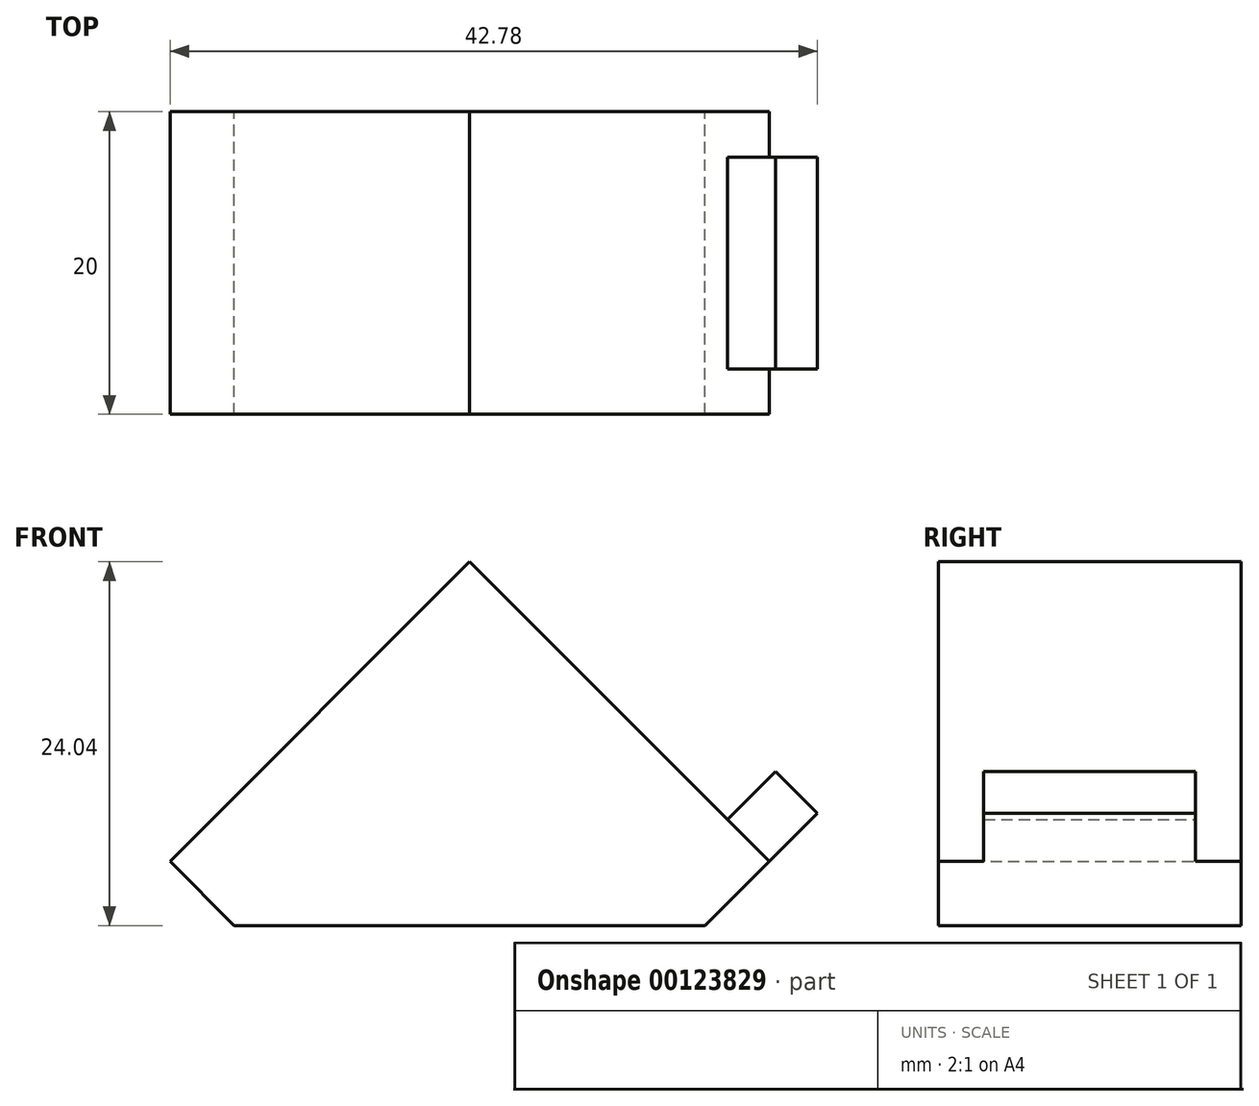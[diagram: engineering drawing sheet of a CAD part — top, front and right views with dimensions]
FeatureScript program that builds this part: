
annotation { "Feature Type Name" : "Feature", "Feature Type Description" : "" }
export const myFeature = defineFeature(function(context is Context, id is Id, definition is map)
    precondition{}
    {
        {
            var Q0;
            Q0=qCreatedBy(makeId("Front.planeOp"),FACE);
            var sketch = newSketch(context, id + "F0", { "sketchPlane" : qUnion([Q0])});
            skLineSegment(sketch, "E0", {"start": v(19.8, 4.24) * mm, "end": v(0, 24.04) * mm});
            skLineSegment(sketch, "E1", {"start": v(0, 24.04) * mm, "end": v(0, 0) * mm, "construction": true});
            skLineSegment(sketch, "E2", {"start": v(0, 0) * mm, "end": v(15.56, 0) * mm});
            skLineSegment(sketch, "E3", {"start": v(19.8, 4.24) * mm, "end": v(15.56, 0) * mm});
            skLineSegment(sketch, "E4.MirrorCS", {"start": v(-19.8, 4.24) * mm, "end": v(0, 24.04) * mm});
            skLineSegment(sketch, "E5.MirrorCS", {"start": v(-19.8, 4.24) * mm, "end": v(-15.56, 0) * mm});
            skLineSegment(sketch, "E6.MirrorCS", {"start": v(0, 0) * mm, "end": v(-15.56, 0) * mm});
            skSolve(sketch);
        }
        {
            var Q0;
            Q0=makeQuery(id+"F0.imprint","IMPRINT",FACE,{"disambiguationData":[TD([[makeQuery(id+"F0.imprint","IMPRINT",EDGE,{"derivedFrom":sQuery(id+"F0.wireOp",EDGE,"E0")}),1.0]])]});
            extrude(context, id + "F1", {"entities" : qUnion([Q0]), "depth" : 20 * mm});
        }
        {
            var Q0;
            Q0=makeQuery(id+"F1.opExtrude","SWEPT_FACE",FACE,{"disambiguationData":[OSD([sQuery(id+"F0.wireOp",EDGE,"E0")])]});
            var sketch = newSketch(context, id + "F2", { "sketchPlane" : qUnion([Q0])});
            skLineSegment(sketch, "E7", {"start": v(5, -2.42) * mm, "end": v(5, -17.05) * mm, "construction": true});
            skLineSegment(sketch, "E8", {"start": v(-17, -10) * mm, "end": v(11, -10) * mm, "construction": true});
            skPoint(sketch, "E9", {"position": v(5, -10) * mm});
            skCircle(sketch, "E10", {"center": v(5, -10) * mm, "radius": 4 * mm});
            skCircle(sketch, "E11", {"center": v(5, -10) * mm, "radius": 2.25 * mm});
            skLineSegment(sketch, "E12.bottom", {"start": v(-17, -7.1) * mm, "end": v(-3, -7.1) * mm});
            skLineSegment(sketch, "E12.top", {"start": v(-17, -12.9) * mm, "end": v(-3, -12.9) * mm});
            skLineSegment(sketch, "E12.left", {"start": v(-17, -7.1) * mm, "end": v(-17, -12.9) * mm});
            skLineSegment(sketch, "E12.right", {"start": v(-3, -7.1) * mm, "end": v(-3, -12.9) * mm});
            skPoint(sketch, "E12.middle", {"position": v(-10, -10) * mm});
            skSolve(sketch);
        }
        {
            var Q0;
            Q0=makeQuery(id+"F2.imprint","IMPRINT",FACE,{"disambiguationData":[TD([[makeQuery(id+"F2.imprint","IMPRINT",EDGE,{"derivedFrom":sQuery(id+"F2.wireOp",EDGE,"E12.bottom")}),-1.0]])]});
            extrude(context, id + "F3", {"entities" : qUnion([Q0]), "operationType" : NewBodyOperationType.ADD, "depth" : 4.5 * mm});
        }
        {
            var Q0;
            Q0=makeQuery(id+"F2.imprint","IMPRINT",FACE,{"disambiguationData":[TD([[makeQuery(id+"F2.imprint","IMPRINT",EDGE,{"derivedFrom":sQuery(id+"F2.wireOp",EDGE,"E10")}),1.0]])]});
            extrude(context, id + "F4", {"entities" : qUnion([Q0]), "operationType" : NewBodyOperationType.REMOVE, "endBound" : BoundingType.THROUGH_ALL, "oppositeDirection" : true, "depth" : 25 * mm, "hasSecondDirection" : true, "secondDirectionOppositeDirection" : true, "secondDirectionDepth" : 6 * mm});
        }
        {
            var Q0;
            Q0=makeQuery(id+"F2.imprint","IMPRINT",FACE,{"disambiguationData":[TD([[makeQuery(id+"F2.imprint","IMPRINT",EDGE,{"derivedFrom":sQuery(id+"F2.wireOp",EDGE,"E11")}),1.0]])]});
            extrude(context, id + "F5", {"entities" : qUnion([Q0]), "operationType" : NewBodyOperationType.REMOVE, "endBound" : BoundingType.THROUGH_ALL, "oppositeDirection" : true, "depth" : 25 * mm});
        }
    });
